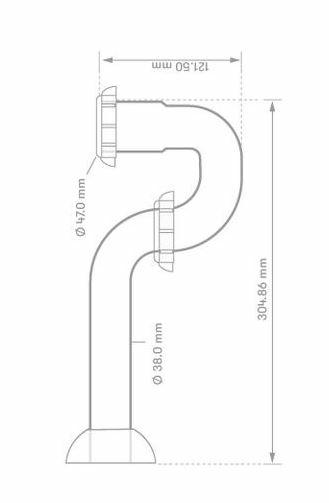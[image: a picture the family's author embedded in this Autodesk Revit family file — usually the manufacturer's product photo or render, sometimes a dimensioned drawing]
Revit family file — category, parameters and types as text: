
# Revit family: 01-9997-11-SIFÓN P PLÁSTICO 1½ Ó 1¼ CROMADO
name_source: partatom
category: Aparatos sanitarios
revit_build: Autodesk Revit 2018 (Build: 20170223_1515(x64)
units: mm (PartAtom-declared; Revit-internal decimal feet)

## family parameters
Anfitrión = Cara
Compartido = No
Corte con vacíos al cargar = No
Cota de conector redondo = Diámetro de uso
Número OmniClass = 23.31.11.00
Punto de cálculo de habitación = No
Tipo de pieza = Normal

## types (1)
- 01-9997-11
    Alto = 121.5 mm
    Ancho = 38 mm  [stored 0.124672 ft]
    Conexión AC = Sí
    Conexión AF = Sí
    Conexión de residuos = No
    Conexión de ventilación = No
    Descripción = Sifon en P
    Elevación por defecto = 0 mm  [stored 0 ft]
    Fabricante = Gricol
    Imagen de tipo = <Ninguno>
    Largo = 304.9 mm  [stored 1.00033 ft]
    Link Ficha Tecnica = http://infotecnica.gricol.com
    Modelo = 01-9997-11
S
    Plastico ABS Cromado = Plastico ABS Cromado
    Product Name = SIFÓN PLÁSTICO 1½ Ó 1¼ CROMADO
    URL = https://www.gricol.com

note: [stored X ft] marks values corroborated as IEEE doubles in the binary element streams (Revit-internal decimal feet)

## geometry (parser evidence)
native form markers: Blend x2, Sweep x2
no freeform markers — native parametric forms only
